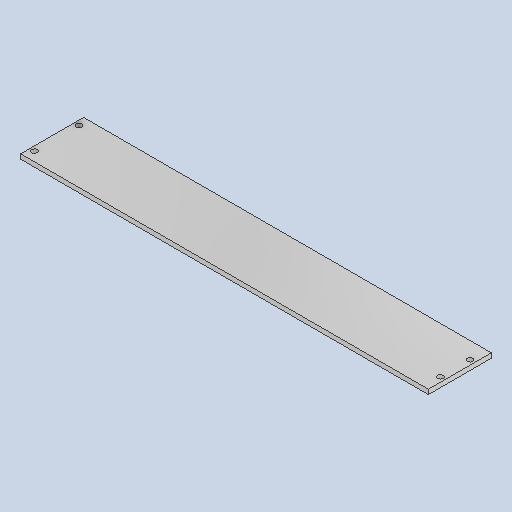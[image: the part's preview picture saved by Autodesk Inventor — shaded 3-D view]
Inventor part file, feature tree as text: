
AUTODESK INVENTOR PART (.ipt)
format: ipt  version: 2025.1 (Build 291241020, 241B)  size: 305,152 bytes
history: native  units: in
note: dims shown in document units (in); Inventor stores cm internally (conversion verified against a paired STEP export)
features: sketch x8, extrude x7, hole x1, projected_geometry x1
ambient origin geometry x8: Origin, YZ Plane, XZ Plane, XY Plane, X Axis, Y Axis, Z Axis, Center Point
bodies: Solid1 (feature_tree)
feature tree (17):
  extrude  "Extrusion1"  Depth=11.0in
  extrude  "Extrusion2"  Depth=1.7in
  extrude  "Extrusion3"  Depth=0.0625in
  extrude  "Extrusion4"  Depth=0.3976in
  extrude  "Extrusion5"  TaperAngle=0.0deg  [1 undecoded]
  extrude  "Extrusion6"  Depth=0.125in
  extrude  "Extrusion7"  Depth=0.6in
  hole  "Hole1"  [1 undecoded]
  sketch  "Sketch1"  dims[d0=11.0in d1=2.5in]
  sketch  "Sketch2"  dims[d2=1.7in d3=0.0in d4=0.0625in]
  sketch  "Sketch3"  dims[d5=0.0625in d6=0.0625in]
  sketch  "Sketch4"  dims[d7=1.5in d8=0.0in d9=0.3976in]
  sketch  "Sketch5"  dims[d10=0.8in d11=0.0in d12=0.0in]
  sketch  "Sketch7"  dims[d13=0.125in d15=0.8in]
  sketch  "Sketch8"  dims[d16=0.4in d17=0.6in]
  projected_geometry  "Projected Loop1"
  sketch  "Sketch9"  dims[d18=0.1875in d19=1.0in d20=0.0in d21=0.125in d22=0.6102in d23=0.6102in d24=1.0in d25=0.0in d26=0.0in d27=0.0in d28=0.125in d29=0.0in d30=0.45in d31=0.125in d32=0.45in d33=0.125in d34=0.125in d35=0.125in d36=0.25in d37=0.25in d38=0.15in d39=0.75in d40=0.5in d41=0.093in d42=0.5635in d43=0.885in d44=0.8108in]
note: 2 required parameter values undecoded (feature->parameter linkage not recoverable at this tier; creation-order binding heuristic only, values carry confidence <= 0.55)
